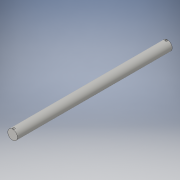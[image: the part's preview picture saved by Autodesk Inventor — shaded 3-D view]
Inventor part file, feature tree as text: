
AUTODESK INVENTOR PART (.ipt)
format: ipt  version: 2016 (Build 200138000, 138)  size: 103,936 bytes
history: native  units: in
note: dims shown in document units (in); Inventor stores cm internally (conversion verified against a paired STEP export)
features: sketch x3, extrude x2
ambient origin geometry x8: Origin, YZ Plane, XZ Plane, XY Plane, X Axis, Y Axis, Z Axis, Center Point
bodies: Solid1 (feature_tree)
feature tree (5):
  extrude  "Extrusion1"  Depth=8.0in TaperAngle=0.0deg
  extrude  "Extrusion4"  Depth=0.06in
  sketch  "Sketch5"  dims[d16=0.1in d17=0.6in d18=0.0in d19=0.1in]
  sketch  "Sketch1"  dims[d0=0.5in d1=8.0in d2=0.0in]
  sketch  "Sketch4"  dims[d13=0.06in d15=0.06in]
